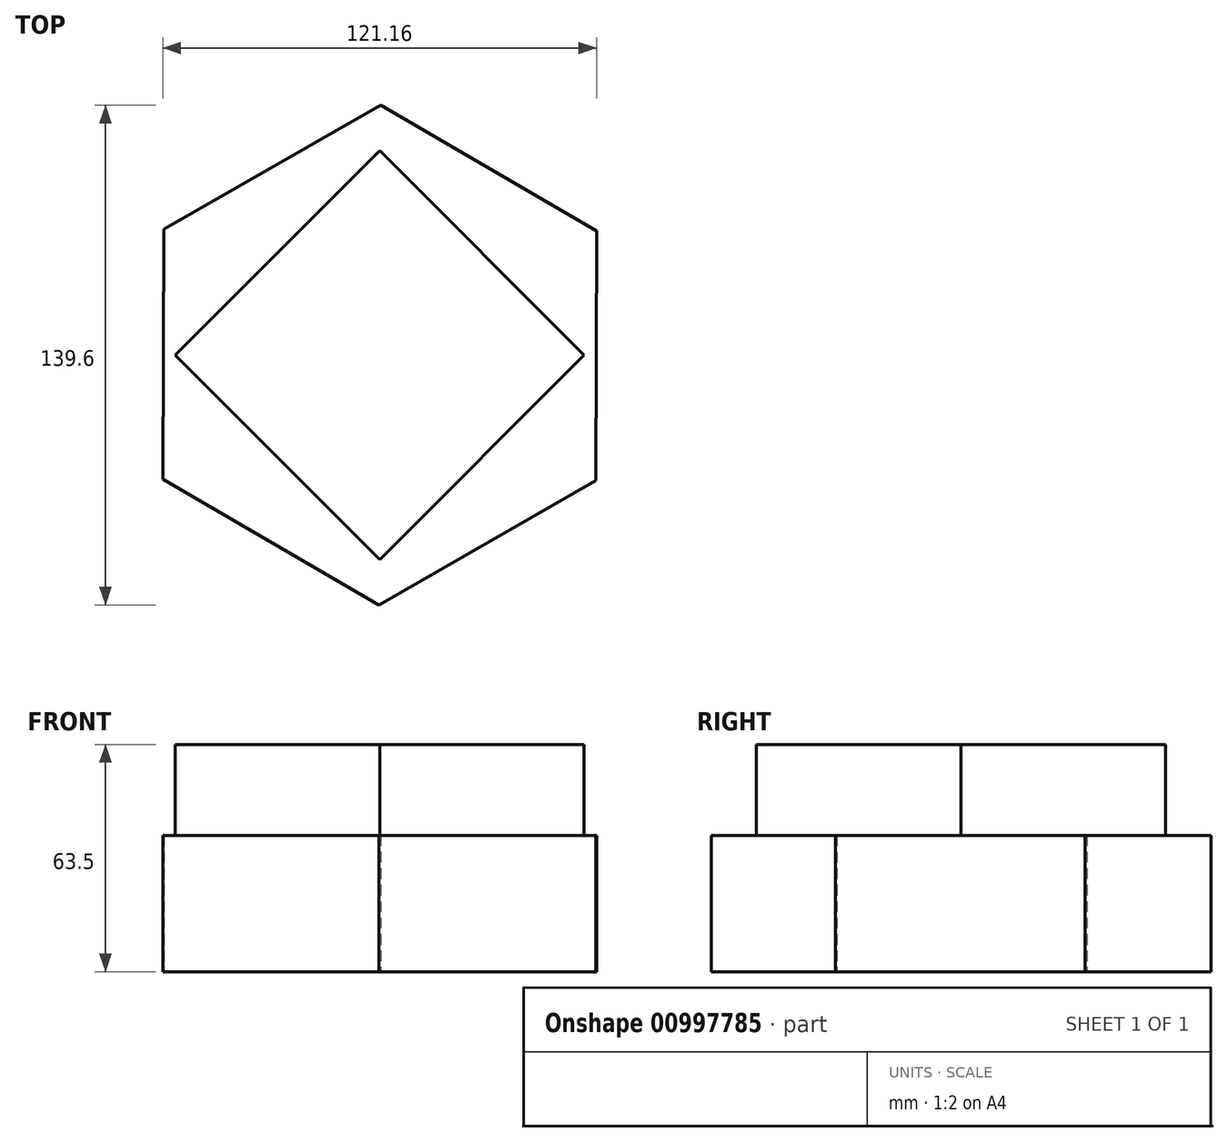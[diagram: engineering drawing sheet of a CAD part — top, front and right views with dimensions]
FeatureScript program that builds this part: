
annotation { "Feature Type Name" : "Feature", "Feature Type Description" : "" }
export const myFeature = defineFeature(function(context is Context, id is Id, definition is map)
    precondition{}
    {
        {
            var Q0;
            Q0=qCreatedBy(makeId("Top.planeOp"),FACE);
            var sketch = newSketch(context, id + "F0", { "sketchPlane" : qUnion([Q0])});
            skCircle(sketch, "E0.cCircle", {"center": v(0, 0) * mm, "radius": 60.45 * mm, "construction": true});
            skLineSegment(sketch, "E0.0", {"start": v(-0.26, -69.8) * mm, "end": v(-60.58, -34.68) * mm});
            skLineSegment(sketch, "E0.1", {"start": v(-60.58, -34.68) * mm, "end": v(-60.32, 35.12) * mm});
            skLineSegment(sketch, "E0.2", {"start": v(-60.32, 35.12) * mm, "end": v(0.26, 69.8) * mm});
            skLineSegment(sketch, "E0.3", {"start": v(0.26, 69.8) * mm, "end": v(60.58, 34.68) * mm});
            skLineSegment(sketch, "E0.4", {"start": v(60.58, 34.68) * mm, "end": v(60.32, -35.12) * mm});
            skLineSegment(sketch, "E0.5", {"start": v(60.32, -35.12) * mm, "end": v(-0.26, -69.8) * mm});
            skPoint(sketch, "E0.0.midPoint", {"position": v(-30.42, -52.24) * mm});
            skSolve(sketch);
        }
        {
            var Q0;
            Q0 = qSketchRegion(id + "F0", true);
            extrude(context, id + "F1", {"entities" : qUnion([Q0]), "depth" : 38.1 * mm, "offsetDistance" : 25.4 * mm});
        }
        {
            var Q0;
            Q0=makeQuery(id+"F1.opExtrude","CAP_FACE",FACE,{"disambiguationData":[OSD([sQuery(id+"F0.wireOp",EDGE,"E0.0"),sQuery(id+"F0.wireOp",EDGE,"E0.1"),sQuery(id+"F0.wireOp",EDGE,"E0.2"),sQuery(id+"F0.wireOp",EDGE,"E0.3"),sQuery(id+"F0.wireOp",EDGE,"E0.4"),sQuery(id+"F0.wireOp",EDGE,"E0.5")])],"isStart":false});
            var sketch = newSketch(context, id + "F2", { "sketchPlane" : qUnion([Q0])});
            skCircle(sketch, "E1.cCircle", {"center": v(0, 0) * mm, "radius": 57.12 * mm, "construction": true});
            skLineSegment(sketch, "E1.0", {"start": v(0, 57.12) * mm, "end": v(57.12, 0) * mm});
            skLineSegment(sketch, "E1.1", {"start": v(57.12, 0) * mm, "end": v(0, -57.12) * mm});
            skLineSegment(sketch, "E1.2", {"start": v(0, -57.12) * mm, "end": v(-57.12, 0) * mm});
            skLineSegment(sketch, "E1.3", {"start": v(-57.12, 0) * mm, "end": v(0, 57.12) * mm});
            skSolve(sketch);
        }
        {
            var Q0;
            Q0=makeQuery(id+"F2.imprint","IMPRINT",FACE,{"disambiguationData":[TD([[makeQuery(id+"F2.imprint","IMPRINT",EDGE,{"derivedFrom":sQuery(id+"F2.wireOp",EDGE,"E1.0")}),-1.0]])]});
            extrude(context, id + "F3", {"entities" : qUnion([Q0]), "operationType" : NewBodyOperationType.ADD, "depth" : 25.4 * mm, "offsetDistance" : 25.4 * mm});
        }
    });
